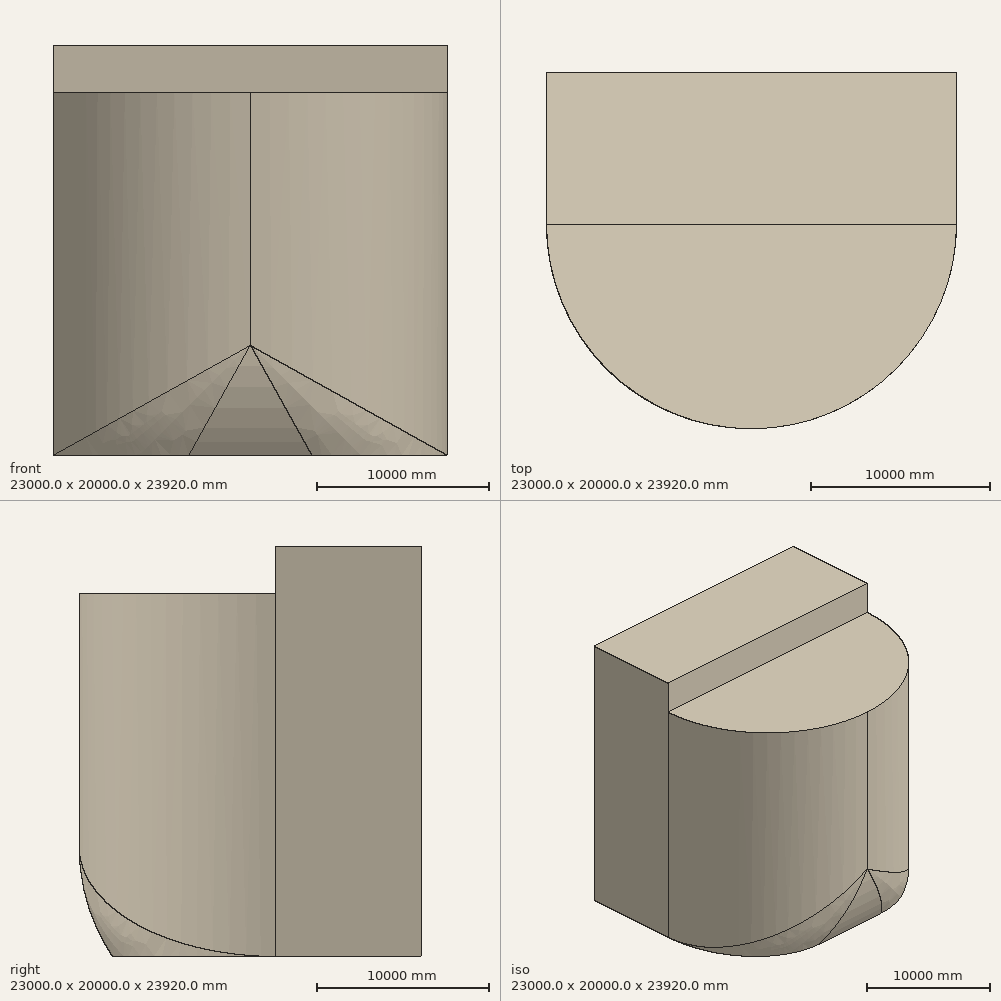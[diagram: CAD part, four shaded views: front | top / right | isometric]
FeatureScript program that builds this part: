
annotation { "Feature Type Name" : "Feature", "Feature Type Description" : "" }
export const myFeature = defineFeature(function(context is Context, id is Id, definition is map)
    precondition{}
    {
        {
            var Q0;
            Q0=qCreatedBy(makeId("Front.planeOp"),FACE);
            var sketch = newSketch(context, id + "F0", { "sketchPlane" : qUnion([Q0])});
            skLineSegment(sketch, "E0", {"start": v(0, 0) * mm, "end": v(6420, 0) * mm});
            skLineSegment(sketch, "E1", {"start": v(11500, 5080) * mm, "end": v(11500, 29000) * mm});
            skLineSegment(sketch, "E2.MirrorCS", {"start": v(0, 0) * mm, "end": v(-6420, 0) * mm});
            skLineSegment(sketch, "E3.MirrorCS", {"start": v(-11500, 5080) * mm, "end": v(-11500, 29000) * mm});
            skLineSegment(sketch, "E4", {"start": v(-11500, 29000) * mm, "end": v(11500, 29000) * mm});
            skPoint(sketch, "E5.visualSharp", {"position": v(-11500, 0) * mm});
            skArc(sketch, "E5.filletArc", {"start": v(-11500, 5080) * mm, "mid": v(-10012.1, 1487.9) * mm, "end": v(-6420, 0) * mm});
            skPoint(sketch, "E6.visualSharp", {"position": v(11500, 0) * mm});
            skArc(sketch, "E6.filletArc", {"start": v(6420, 0) * mm, "mid": v(10012.1, 1487.9) * mm, "end": v(11500, 5080) * mm});
            skLineSegment(sketch, "E7", {"start": v(0, 29000) * mm, "end": v(0, 19000) * mm});
            skPoint(sketch, "E7.endSnap0", {"position": v(0, 29000) * mm});
            skLineSegment(sketch, "E8", {"start": v(0, 19000) * mm, "end": v(-11500, 19000) * mm});
            skLineSegment(sketch, "E9", {"start": v(0, 19000) * mm, "end": v(11500, 19000) * mm});
            skLineSegment(sketch, "E10", {"start": v(0, 19000) * mm, "end": v(0, 0) * mm});
            skSolve(sketch);
        }
        {
            var Q0;
            {var subQ4=sQuery(id+"F0.wireOp",EDGE,"E7");Q0=makeQuery(id+"F0.imprint","IMPRINT",FACE,{"disambiguationData":[TD([[makeQuery(id+"F0.imprint","IMPRINT",EDGE,{"derivedFrom":subQ4}),-1.0]])]});}
            var Q1;
            Q1=makeQuery(id+"F0.imprint","IMPRINT",FACE,{"disambiguationData":[TD([[makeQuery(id+"F0.imprint","IMPRINT",EDGE,{"derivedFrom":sQuery(id+"F0.wireOp",EDGE,"E2.MirrorCS")}),-1.0]])]});
            var Q2;
            Q2=makeQuery(id+"F0.imprint","IMPRINT",FACE,{"disambiguationData":[TD([[makeQuery(id+"F0.imprint","IMPRINT",EDGE,{"derivedFrom":sQuery(id+"F0.wireOp",EDGE,"E0")}),1.0]])]});
            var Q3;
            {var subQ4=sQuery(id+"F0.wireOp",EDGE,"E7");Q3=makeQuery(id+"F0.imprint","IMPRINT",FACE,{"disambiguationData":[TD([[makeQuery(id+"F0.imprint","IMPRINT",EDGE,{"derivedFrom":subQ4}),1.0]])]});}
            extrude(context, id + "F1", {"entities" : qUnion([Q0, Q1, Q2, Q3]), "depth" : 20000 * mm});
        }
        {
            var Q0;
            Q0=makeQuery(id+"F1.opExtrude","CAP_EDGE",EDGE,{"disambiguationData":[OSD([sQuery(id+"F0.wireOp",EDGE,"E3.MirrorCS")])],"isStart":false});
            var Q1;
            Q1=makeQuery(id+"F1.opExtrude","CAP_EDGE",EDGE,{"disambiguationData":[OSD([sQuery(id+"F0.wireOp",EDGE,"E1")])],"isStart":false});
            fillet(context, id + "F2", {"entities" : qUnion([Q0, Q1]), "radius" : 11480.8 * mm, "tangentPropagation" : true, "allowEdgeOverflow" : false});
        }
        {
            var Q0;
            Q0=makeQuery(id+"F1.opExtrude","CAP_FACE",FACE,{"disambiguationData":[OSD([sQuery(id+"F0.wireOp",EDGE,"E0"),sQuery(id+"F0.wireOp",EDGE,"E1"),sQuery(id+"F0.wireOp",EDGE,"E2.MirrorCS"),sQuery(id+"F0.wireOp",EDGE,"E3.MirrorCS"),sQuery(id+"F0.wireOp",EDGE,"E4"),sQuery(id+"F0.wireOp",EDGE,"E5.filletArc"),sQuery(id+"F0.wireOp",EDGE,"E6.filletArc")])],"isStart":true});
            var sketch = newSketch(context, id + "F3", { "sketchPlane" : qUnion([Q0])});
            skLineSegment(sketch, "E11", {"start": v(-11500, 5080) * mm, "end": v(11500, 5080) * mm});
            skSolve(sketch);
        }
        {
            var Q0;
            Q0=makeQuery(id+"F3.imprint","IMPRINT",FACE,{"disambiguationData":[TD([[makeQuery(id+"F3.imprint","IMPRINT",EDGE,{"derivedFrom":sQuery(id+"F3.wireOp",EDGE,"E11")}),-1.0]])]});
            extrude(context, id + "F4", {"entities" : qUnion([Q0]), "operationType" : NewBodyOperationType.REMOVE, "oppositeDirection" : true, "depth" : 20000 * mm});
        }
        {
            var Q0;
            Q0=makeQuery(id+"F1.opExtrude","SWEPT_FACE",FACE,{"disambiguationData":[OSD([sQuery(id+"F0.wireOp",EDGE,"E4")])]});
            var sketch = newSketch(context, id + "F5", { "sketchPlane" : qUnion([Q0])});
            skLineSegment(sketch, "E12", {"start": v(-11500, -8519.2) * mm, "end": v(11500, -8519.2) * mm});
            skSolve(sketch);
        }
        {
            var Q0;
            Q0=makeQuery(id+"F5.imprint","IMPRINT",FACE,{"disambiguationData":[TD([[makeQuery(id+"F5.imprint","IMPRINT",EDGE,{"derivedFrom":sQuery(id+"F5.wireOp",EDGE,"E12")}),-1.0]])]});
            extrude(context, id + "F6", {"entities" : qUnion([Q0]), "operationType" : NewBodyOperationType.REMOVE, "oppositeDirection" : true, "depth" : 2743.2 * mm});
        }
    });
